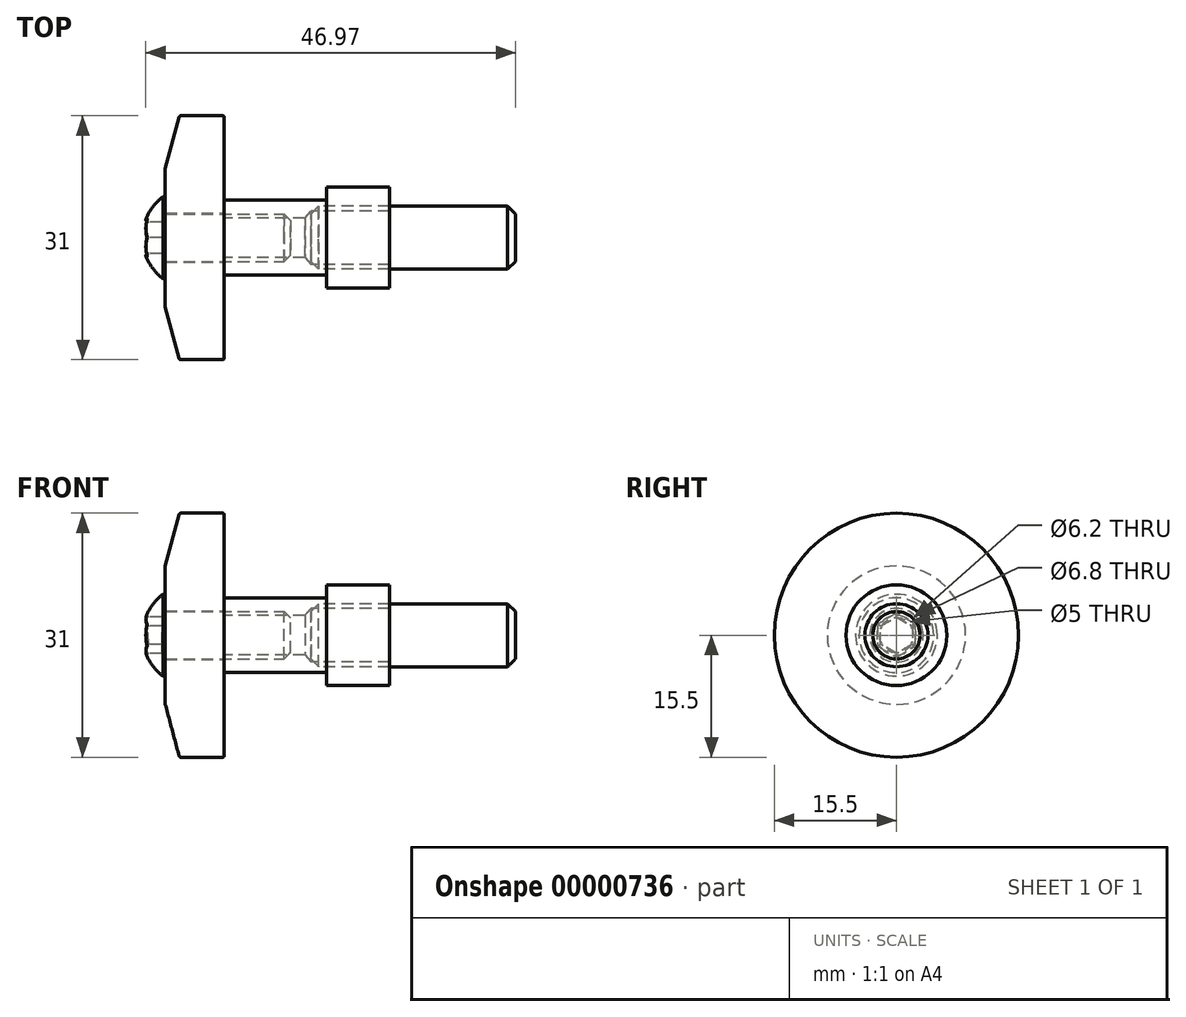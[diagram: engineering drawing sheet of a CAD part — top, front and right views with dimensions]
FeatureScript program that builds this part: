
annotation { "Feature Type Name" : "Feature", "Feature Type Description" : "" }
export const myFeature = defineFeature(function(context is Context, id is Id, definition is map)
    precondition{}
    {
        {
            var Q0;
            Q0=qCreatedBy(makeId("Front.planeOp"),FACE);
            var sketch = newSketch(context, id + "F0", { "sketchPlane" : qUnion([Q0])});
            skLineSegment(sketch, "E0", {"start": v(0, 3.4) * mm, "end": v(0, 6.4) * mm});
            skLineSegment(sketch, "E1", {"start": v(0, 6.4) * mm, "end": v(-8, 6.4) * mm});
            skLineSegment(sketch, "E2", {"start": v(-8, 6.4) * mm, "end": v(-8, 4.75) * mm});
            skLineSegment(sketch, "E3", {"start": v(-8, 4.75) * mm, "end": v(-21, 4.75) * mm});
            skLineSegment(sketch, "E4", {"start": v(-21, 4.75) * mm, "end": v(-21, 2.5) * mm});
            skLineSegment(sketch, "E5", {"start": v(-21, 2.5) * mm, "end": v(-10.76, 2.5) * mm});
            skLineSegment(sketch, "E6", {"start": v(-10.76, 2.5) * mm, "end": v(-10, 3.4) * mm});
            skLineSegment(sketch, "E7", {"start": v(-10, 3.4) * mm, "end": v(0, 3.4) * mm});
            skLineSegment(sketch, "E8", {"start": v(0, 3.4) * mm, "end": v(0, 0) * mm, "construction": true});
            skLineSegment(sketch, "E9", {"start": v(0, 0) * mm, "end": v(22.18, 0) * mm, "construction": true});
            skSolve(sketch);
        }
        {
            var Q0;
            Q0=makeQuery(id+"F0.imprint","IMPRINT",FACE,{"disambiguationData":[TD([[makeQuery(id+"F0.imprint","IMPRINT",EDGE,{"derivedFrom":sQuery(id+"F0.wireOp",EDGE,"E0")}),1.0]])]});
            var Q1;
            Q1=sQuery(id+"F0.wireOp",EDGE,"E9");
            revolve(context, id + "F1", {"entities" : qUnion([Q0]), "axis" : qUnion([Q1]), "revolveType" : RevolveType.FULL});
        }
        {
            var Q0;
            Q0=qCreatedBy(makeId("Front.planeOp"),FACE);
            var sketch = newSketch(context, id + "F2", { "sketchPlane" : qUnion([Q0])});
            skLineSegment(sketch, "E10", {"start": v(-21, 3.1) * mm, "end": v(-21, 15.5) * mm});
            skLineSegment(sketch, "E11", {"start": v(-21, 15.5) * mm, "end": v(-26.7, 15.5) * mm});
            skLineSegment(sketch, "E12", {"start": v(-26.7, 15.5) * mm, "end": v(-28.5, 8.78) * mm});
            skLineSegment(sketch, "E13", {"start": v(-28.5, 8.78) * mm, "end": v(-28.5, 3.1) * mm});
            skLineSegment(sketch, "E14", {"start": v(-28.5, 0) * mm, "end": v(-35.31, 0) * mm, "construction": true});
            skLineSegment(sketch, "E15", {"start": v(-28.5, 3.1) * mm, "end": v(-21, 3.1) * mm});
            skPoint(sketch, "E16.orphan", {"position": v(-21, 0) * mm});
            skSolve(sketch);
        }
        {
            var Q0;
            Q0=makeQuery(id+"F2.imprint","IMPRINT",FACE,{"disambiguationData":[TD([[makeQuery(id+"F2.imprint","IMPRINT",EDGE,{"derivedFrom":sQuery(id+"F2.wireOp",EDGE,"E10")}),1.0]])]});
            var Q1;
            Q1=sQuery(id+"F2.wireOp",EDGE,"E14");
            revolve(context, id + "F3", {"entities" : qUnion([Q0]), "axis" : qUnion([Q1]), "revolveType" : RevolveType.FULL});
        }
        {
            var Q0;
            Q0=makeQuery(id+"F3.opRevolve","SWEPT_EDGE",EDGE,{"disambiguationData":[OSD([sQuery(id+"F2.wireOp",EDGE,"E11"),sQuery(id+"F2.wireOp",EDGE,"E12")])]});
            var Q1;
            Q1=makeQuery(id+"F3.opRevolve","SWEPT_EDGE",EDGE,{"disambiguationData":[OSD([sQuery(id+"F2.wireOp",EDGE,"E10"),sQuery(id+"F2.wireOp",EDGE,"E11")])]});
            fillet(context, id + "F4", {"entities" : qUnion([Q0, Q1]), "radius" : .2 * mm, "tangentPropagation" : true, "allowEdgeOverflow" : false});
        }
        {
            var Q0;
            Q0=qCreatedBy(makeId("Front.planeOp"),FACE);
            var sketch = newSketch(context, id + "F5", { "sketchPlane" : qUnion([Q0])});
            skLineSegment(sketch, "E17", {"start": v(-10, 4) * mm, "end": v(-10, 0) * mm});
            skLineSegment(sketch, "E18", {"start": v(-10, 4) * mm, "end": v(16, 4) * mm});
            skLineSegment(sketch, "E19", {"start": v(16, 4) * mm, "end": v(16, 0) * mm});
            skLineSegment(sketch, "E20", {"start": v(16, 0) * mm, "end": v(-10, 0) * mm});
            skLineSegment(sketch, "E21", {"start": v(0, 0) * mm, "end": v(29.18, 0) * mm, "construction": true});
            skSolve(sketch);
        }
        {
            var Q0;
            Q0=makeQuery(id+"F5.imprint","IMPRINT",FACE,{"disambiguationData":[TD([[makeQuery(id+"F5.imprint","IMPRINT",EDGE,{"derivedFrom":sQuery(id+"F5.wireOp",EDGE,"E17")}),1.0]])]});
            var Q1;
            Q1=sQuery(id+"F5.wireOp",EDGE,"E21");
            revolve(context, id + "F6", {"entities" : qUnion([Q0]), "axis" : qUnion([Q1]), "revolveType" : RevolveType.FULL});
        }
        {
            var Q0;
            Q0=makeQuery(id+"F6.opRevolve","SWEPT_EDGE",EDGE,{"disambiguationData":[OSD([sQuery(id+"F5.wireOp",EDGE,"E18"),sQuery(id+"F5.wireOp",EDGE,"E19")])]});
            var Q1;
            Q1=makeQuery(id+"F6.opRevolve","SWEPT_EDGE",EDGE,{"disambiguationData":[OSD([sQuery(id+"F5.wireOp",EDGE,"E17"),sQuery(id+"F5.wireOp",EDGE,"E18")])]});
            chamfer(context, id + "F7", {"entities" : qUnion([Q0, Q1]), "width" : 1 * mm, "tangentPropagation" : true});
        }
        {
            var Q0;
            Q0=qCreatedBy(makeId("Front.planeOp"),FACE);
            var sketch = newSketch(context, id + "F8", { "sketchPlane" : qUnion([Q0])});
            skLineSegment(sketch, "E22", {"start": v(-12.6, 0) * mm, "end": v(-12.6, 3) * mm});
            skLineSegment(sketch, "E23", {"start": v(-12.6, 3) * mm, "end": v(-28.5, 3) * mm});
            skLineSegment(sketch, "E24", {"start": v(-28.5, 3) * mm, "end": v(-28.5, 5.2) * mm});
            skLineSegment(sketch, "E25", {"start": v(-28.5, 5.2) * mm, "end": v(-28.8, 5.2) * mm});
            skLineSegment(sketch, "E26", {"start": v(-31.5, 0) * mm, "end": v(-12.6, 0) * mm});
            skLineSegment(sketch, "E27", {"start": v(-31.5, 0) * mm, "end": v(-38, 0) * mm, "construction": true});
            skArc(sketch, "E28", {"start": v(-28.8, 5.2) * mm, "mid": v(-30.72, 2.9) * mm, "end": v(-31.5, 0) * mm});
            skSolve(sketch);
        }
        {
            var Q0;
            Q0=makeQuery(id+"F8.imprint","IMPRINT",FACE,{"disambiguationData":[TD([[makeQuery(id+"F8.imprint","IMPRINT",EDGE,{"derivedFrom":sQuery(id+"F8.wireOp",EDGE,"E22")}),1.0]])]});
            var Q1;
            Q1=sQuery(id+"F8.wireOp",EDGE,"E27");
            revolve(context, id + "F9", {"entities" : qUnion([Q0]), "axis" : qUnion([Q1]), "revolveType" : RevolveType.FULL});
        }
        {
            var Q0;
            Q0=makeQuery(id+"F9.opRevolve","SWEPT_EDGE",EDGE,{"disambiguationData":[OSD([sQuery(id+"F8.wireOp",EDGE,"E22"),sQuery(id+"F8.wireOp",EDGE,"E23")])]});
            chamfer(context, id + "F10", {"entities" : qUnion([Q0]), "width" : .8 * mm, "tangentPropagation" : true});
        }
        {
            var Q0;
            Q0=makeQuery(id+"F9.opRevolve","SWEPT_FACE",FACE,{"disambiguationData":[OSD([sQuery(id+"F8.wireOp",EDGE,"E24")])]});
            cPlane(context, id + "F11", {"entities" : qUnion([Q0]), "cplaneType" : CPlaneType.OFFSET, "offset" : 3 * mm, "oppositeDirection" : true, "width" : 150 * mm, "height" : 150 * mm});
        }
        {
            var Q0;
            Q0=qCreatedBy(id+"F11.planeOp",FACE);
            var sketch = newSketch(context, id + "F12", { "sketchPlane" : qUnion([Q0])});
            skCircle(sketch, "E29.cCircle", {"center": v(0, 0) * mm, "radius": 2 * mm, "construction": true});
            skLineSegment(sketch, "E29.0", {"start": v(-2, -1.15) * mm, "end": v(-2, 1.15) * mm});
            skLineSegment(sketch, "E29.1", {"start": v(-2, 1.15) * mm, "end": v(0, 2.3) * mm});
            skLineSegment(sketch, "E29.2", {"start": v(0, 2.3) * mm, "end": v(2, 1.15) * mm});
            skLineSegment(sketch, "E29.3", {"start": v(2, 1.15) * mm, "end": v(2, -1.15) * mm});
            skLineSegment(sketch, "E29.4", {"start": v(2, -1.15) * mm, "end": v(0, -2.3) * mm});
            skLineSegment(sketch, "E29.5", {"start": v(0, -2.3) * mm, "end": v(-2, -1.15) * mm});
            skPoint(sketch, "E29.0.midPoint", {"position": v(-2, 0) * mm});
            skSolve(sketch);
        }
        {
            var Q0;
            Q0=makeQuery(id+"F12.imprint","IMPRINT",FACE,{"disambiguationData":[TD([[makeQuery(id+"F12.imprint","IMPRINT",EDGE,{"derivedFrom":sQuery(id+"F12.wireOp",EDGE,"E29.0")}),-1.0]])]});
            extrude(context, id + "F13", {"entities" : qUnion([Q0]), "operationType" : NewBodyOperationType.REMOVE, "depth" : 2.6 * mm});
        }
        {
            var Q0;
            Q0=makeQuery(id+"F13.boolean.opBoolean","INTERSECT",EDGE,{"derivedFrom":[makeQuery(id+"F9.opRevolve","SWEPT_FACE",FACE,{"disambiguationData":[OSD([sQuery(id+"F8.wireOp",EDGE,"E28")])]}),makeQuery(id+"F13.opExtrude","SWEPT_FACE",FACE,{"disambiguationData":[OSD([sQuery(id+"F12.wireOp",EDGE,"E29.2")])]})]});
            var Q1;
            Q1=makeQuery(id+"F13.boolean.opBoolean","INTERSECT",EDGE,{"derivedFrom":[makeQuery(id+"F9.opRevolve","SWEPT_FACE",FACE,{"disambiguationData":[OSD([sQuery(id+"F8.wireOp",EDGE,"E28")])]}),makeQuery(id+"F13.opExtrude","SWEPT_FACE",FACE,{"disambiguationData":[OSD([sQuery(id+"F12.wireOp",EDGE,"E29.3")])]})]});
            var Q2;
            Q2=makeQuery(id+"F13.boolean.opBoolean","INTERSECT",EDGE,{"derivedFrom":[makeQuery(id+"F9.opRevolve","SWEPT_FACE",FACE,{"disambiguationData":[OSD([sQuery(id+"F8.wireOp",EDGE,"E28")])]}),makeQuery(id+"F13.opExtrude","SWEPT_FACE",FACE,{"disambiguationData":[OSD([sQuery(id+"F12.wireOp",EDGE,"E29.4")])]})]});
            var Q3;
            Q3=makeQuery(id+"F13.boolean.opBoolean","INTERSECT",EDGE,{"derivedFrom":[makeQuery(id+"F9.opRevolve","SWEPT_FACE",FACE,{"disambiguationData":[OSD([sQuery(id+"F8.wireOp",EDGE,"E28")])]}),makeQuery(id+"F13.opExtrude","SWEPT_FACE",FACE,{"disambiguationData":[OSD([sQuery(id+"F12.wireOp",EDGE,"E29.5")])]})]});
            var Q4;
            Q4=makeQuery(id+"F13.boolean.opBoolean","INTERSECT",EDGE,{"derivedFrom":[makeQuery(id+"F9.opRevolve","SWEPT_FACE",FACE,{"disambiguationData":[OSD([sQuery(id+"F8.wireOp",EDGE,"E28")])]}),makeQuery(id+"F13.opExtrude","SWEPT_FACE",FACE,{"disambiguationData":[OSD([sQuery(id+"F12.wireOp",EDGE,"E29.0")])]})]});
            var Q5;
            Q5=makeQuery(id+"F13.boolean.opBoolean","INTERSECT",EDGE,{"derivedFrom":[makeQuery(id+"F9.opRevolve","SWEPT_FACE",FACE,{"disambiguationData":[OSD([sQuery(id+"F8.wireOp",EDGE,"E28")])]}),makeQuery(id+"F13.opExtrude","SWEPT_FACE",FACE,{"disambiguationData":[OSD([sQuery(id+"F12.wireOp",EDGE,"E29.1")])]})]});
            fillet(context, id + "F14", {"entities" : qUnion([Q0, Q1, Q2, Q3, Q4, Q5]), "radius" : .3 * mm, "tangentPropagation" : true, "allowEdgeOverflow" : false});
        }
    });
